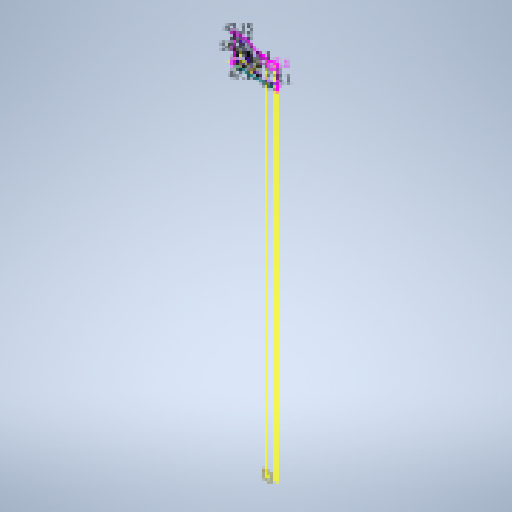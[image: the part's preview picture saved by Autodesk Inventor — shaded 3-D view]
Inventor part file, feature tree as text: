
AUTODESK INVENTOR PART (.ipt)
format: ipt  version: 2023.2 (Build 272271000, 271)  size: 198,656 bytes
history: native  units: mm
features: reference x25, other x4, plane x2, sketch x1
ambient origin geometry x8: Origin, YZ Plane, XZ Plane, XY Plane, X Axis, Y Axis, Z Axis, Center Point
feature tree (32):
  plane  "Work Plane1"
  sketch  "Sketch1"  dims[d0=5.1mm d2=5.1mm d9=5.1mm d10=15.0mm d11=15.0mm d17=47.15mm d22=5.0mm d23=5.0mm d24=5.0mm d29=20.0mm d30=6.0mm d31=47.15mm d32=22.1mm d33=5.1mm d34=5.1mm d35=5.1mm d36=5.1mm d37=5.1mm]
  plane  "Work Plane2"
  reference  "Reference1"
  reference  "Reference2"
  reference  "Reference3"
  reference  "Reference4"
  reference  "Reference5"
  reference  "Reference6"
  reference  "Reference7"
  reference  "Reference8"
  reference  "Reference9"
  reference  "Reference10"
  reference  "Reference11"
  reference  "Reference12"
  reference  "Reference13"
  reference  "Reference14"
  reference  "Reference15"
  reference  "Reference16"
  reference  "Reference17"
  reference  "Reference18"
  reference  "Reference19"
  reference  "Reference20"
  reference  "Reference21"
  reference  "Reference22"
  reference  "Reference23"
  reference  "Reference24"
  reference  "Reference25"
  parser-record x1  (decoder bookkeeping rows leaked as tree rows — omitted from the tree; the rows remain in map.json)
  other  "Main Assembly.iam"
  other  "C beam extrusion 250:2"
  other  "20x40 1000:1"
note: 1 file-system path scrubbed to <path> (originals preserved in map.json)
